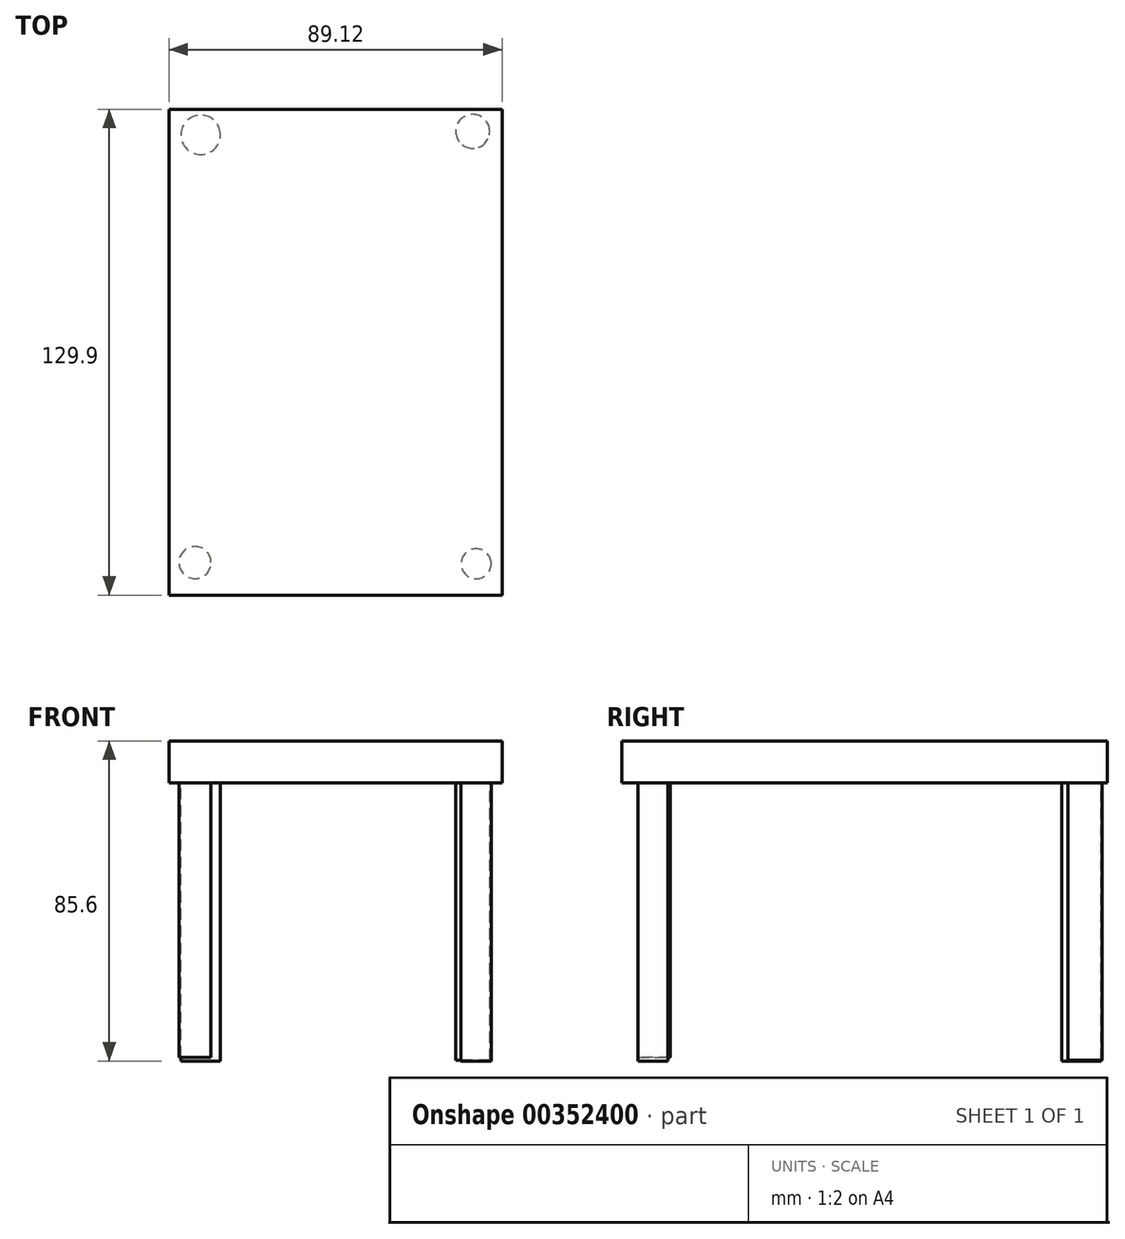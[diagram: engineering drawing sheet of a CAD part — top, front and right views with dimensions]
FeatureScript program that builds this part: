
annotation { "Feature Type Name" : "Feature", "Feature Type Description" : "" }
export const myFeature = defineFeature(function(context is Context, id is Id, definition is map)
    precondition{}
    {
        {
            var Q0;
            Q0=qCreatedBy(makeId("Top.planeOp"),FACE);
            var sketch = newSketch(context, id + "F0", { "sketchPlane" : qUnion([Q0])});
            skLineSegment(sketch, "E0.bottom", {"start": v(44.56, 64.95) * mm, "end": v(-44.56, 64.95) * mm});
            skLineSegment(sketch, "E0.top", {"start": v(44.56, -64.95) * mm, "end": v(-44.56, -64.95) * mm});
            skLineSegment(sketch, "E0.left", {"start": v(44.56, 64.95) * mm, "end": v(44.56, -64.95) * mm});
            skLineSegment(sketch, "E0.right", {"start": v(-44.56, 64.95) * mm, "end": v(-44.56, -64.95) * mm});
            skPoint(sketch, "E0.middle", {"position": v(0, 0) * mm});
            skSolve(sketch);
        }
        {
            var Q0;
            Q0 = qSketchRegion(id + "F0", true);
            extrude(context, id + "F1", {"entities" : qUnion([Q0]), "depth" : 11.18 * mm});
        }
        {
            var Q0;
            Q0=qCreatedBy(makeId("Top.planeOp"),FACE);
            var sketch = newSketch(context, id + "F2", { "sketchPlane" : qUnion([Q0])});
            skCircle(sketch, "E1", {"center": v(-36.07, 58.12) * mm, "radius": 5.28 * mm});
            skSolve(sketch);
        }
        {
            var Q0;
            Q0=makeQuery(id+"F1.opExtrude","CAP_FACE",FACE,{"disambiguationData":[OSD([sQuery(id+"F0.wireOp",EDGE,"E0.bottom"),sQuery(id+"F0.wireOp",EDGE,"E0.top"),sQuery(id+"F0.wireOp",EDGE,"E0.left"),sQuery(id+"F0.wireOp",EDGE,"E0.right")])],"isStart":true});
            var sketch = newSketch(context, id + "F3", { "sketchPlane" : qUnion([Q0])});
            skCircle(sketch, "E2", {"center": v(36.7, -59.04) * mm, "radius": 4.55 * mm});
            skSolve(sketch);
        }
        {
            var Q0;
            Q0=qCreatedBy(makeId("Top.planeOp"),FACE);
            var sketch = newSketch(context, id + "F4", { "sketchPlane" : qUnion([Q0])});
            skCircle(sketch, "E3", {"center": v(-37.62, -56.27) * mm, "radius": 4.3 * mm});
            skSolve(sketch);
        }
        {
            var Q0;
            Q0=qCreatedBy(makeId("Top.planeOp"),FACE);
            var sketch = newSketch(context, id + "F5", { "sketchPlane" : qUnion([Q0])});
            skCircle(sketch, "E4", {"center": v(37.62, -56.58) * mm, "radius": 4.02 * mm});
            skSolve(sketch);
        }
        {
            var Q0;
            Q0 = qSketchRegion(id + "F2", true);
            extrude(context, id + "F6", {"entities" : qUnion([Q0]), "operationType" : NewBodyOperationType.ADD, "oppositeDirection" : true, "depth" : 74.42 * mm});
        }
        {
            var Q0;
            Q0 = qSketchRegion(id + "F3", true);
            extrude(context, id + "F7", {"entities" : qUnion([Q0]), "operationType" : NewBodyOperationType.ADD, "depth" : 74.17 * mm});
        }
        {
            var Q0;
            Q0 = qSketchRegion(id + "F4", true);
            extrude(context, id + "F8", {"entities" : qUnion([Q0]), "operationType" : NewBodyOperationType.ADD, "oppositeDirection" : true, "depth" : 73.4 * mm});
        }
        {
            var Q0;
            Q0 = qSketchRegion(id + "F5", true);
            extrude(context, id + "F9", {"entities" : qUnion([Q0]), "operationType" : NewBodyOperationType.ADD, "oppositeDirection" : true, "depth" : 74.42 * mm});
        }
    });
